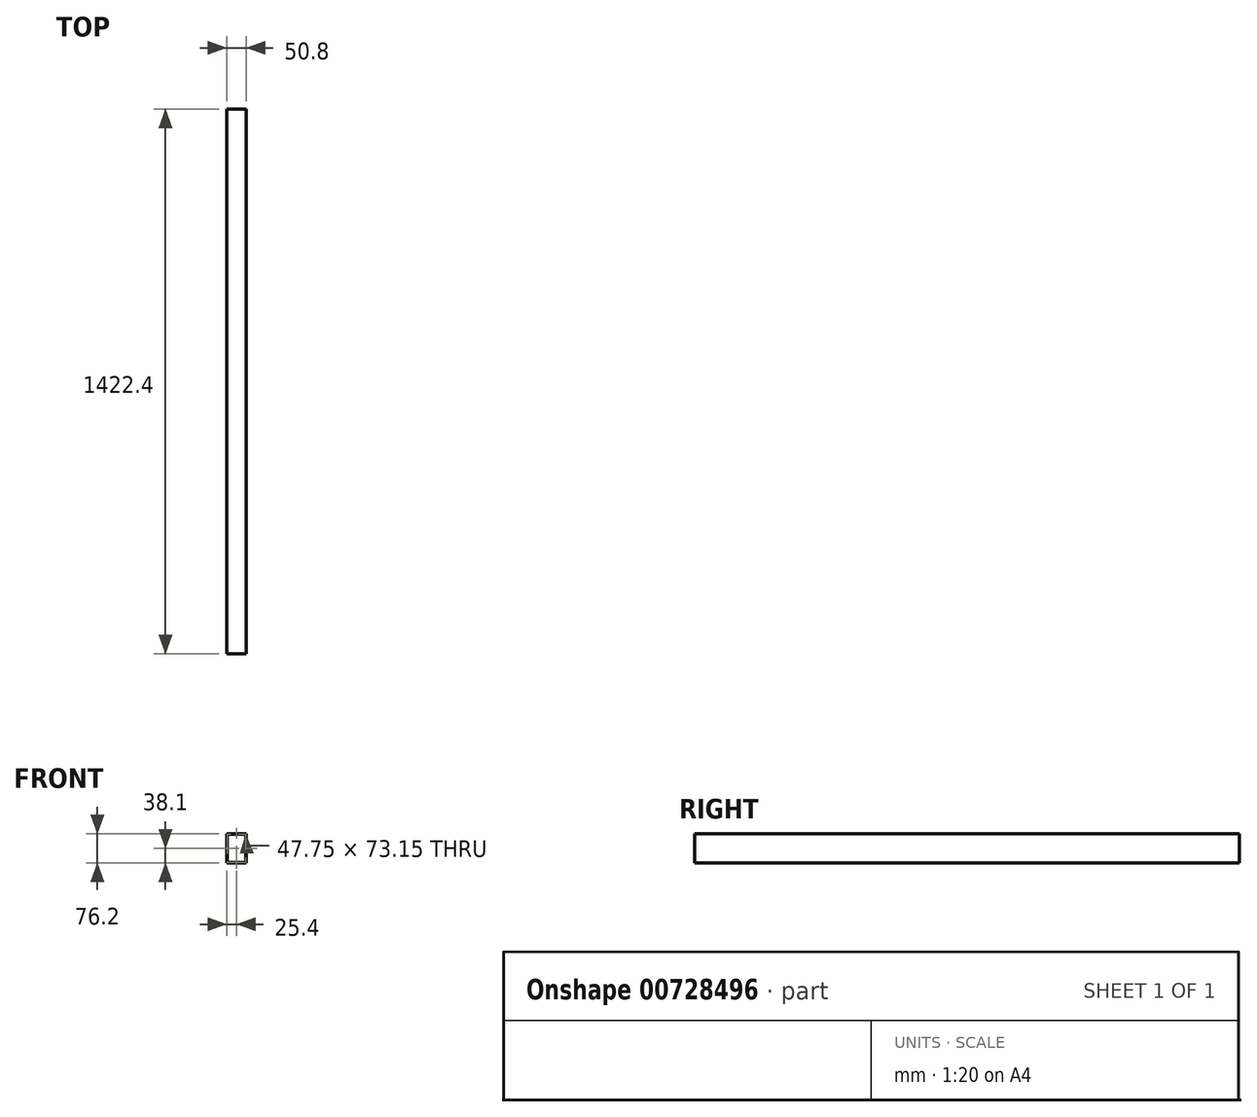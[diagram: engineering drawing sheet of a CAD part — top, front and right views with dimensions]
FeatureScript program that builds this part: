
annotation { "Feature Type Name" : "Feature", "Feature Type Description" : "" }
export const myFeature = defineFeature(function(context is Context, id is Id, definition is map)
    precondition{}
    {
        {
            var Q0;
            Q0=qCreatedBy(makeId("Front.planeOp"),FACE);
            var sketch = newSketch(context, id + "F0", { "sketchPlane" : qUnion([Q0])});
            skLineSegment(sketch, "E0.bottom", {"start": v(-25.4, 38.1) * mm, "end": v(25.4, 38.1) * mm});
            skLineSegment(sketch, "E0.top", {"start": v(-25.4, -38.1) * mm, "end": v(25.4, -38.1) * mm});
            skLineSegment(sketch, "E0.left", {"start": v(-25.4, 38.1) * mm, "end": v(-25.4, -38.1) * mm});
            skLineSegment(sketch, "E0.right", {"start": v(25.4, 38.1) * mm, "end": v(25.4, -38.1) * mm});
            skPoint(sketch, "E0.middle", {"position": v(0, 0) * mm});
            skLineSegment(sketch, "E1.bottom", {"start": v(-23.88, 36.58) * mm, "end": v(23.88, 36.58) * mm});
            skLineSegment(sketch, "E1.top", {"start": v(-23.88, -36.58) * mm, "end": v(23.88, -36.58) * mm});
            skLineSegment(sketch, "E1.left", {"start": v(-23.88, 36.58) * mm, "end": v(-23.88, -36.58) * mm});
            skLineSegment(sketch, "E1.right", {"start": v(23.88, 36.58) * mm, "end": v(23.88, -36.58) * mm});
            skSolve(sketch);
        }
        {
            var Q0;
            Q0=makeQuery(id+"F0.imprint","IMPRINT",FACE,{"disambiguationData":[TD([[makeQuery(id+"F0.imprint","IMPRINT",EDGE,{"derivedFrom":sQuery(id+"F0.wireOp",EDGE,"E0.bottom")}),-1.0]])]});
            extrude(context, id + "F1", {"entities" : qUnion([Q0]), "endBound" : BoundingType.SYMMETRIC, "depth" : 1422.4 * mm, "offsetDistance" : 25.4 * mm});
        }
    });
